# Revit family: CENTUM Winkel 3-Loch, quer ab XL100
name_source: partatom
category: HLS-Bauteile
revit_build: Autodesk Revit 2017 (Build: 20190507_1515(x64)
units: mm (PartAtom-declared; Revit-internal decimal feet)

## family parameters
Arbeitsebenenbasiert = Ja
Beim Laden mit Abzugskörper schneiden = Nein
Bemaßung runder Anschluss = Durchmesser verwenden
Gemeinsam genutzt = Ja
Immer vertikal = Nein
Raumberechnungspunkt = Nein
Teiletyp = Normal

## types (2) — shared parameters
B = 90 mm  [stored 0.295276 ft]
Breite Material = 90 mm
Fabrikat = MEFA
Firma = MEFA Befestigungs- und Montagesysteme GmbH
Gewicht = 1.74 kg
Gewicht pro Bauteil = 1.74 kg
Kurztext2 = 90 ° Schenkel 150 x 100 mm
L1 = 150 mm
L2 = 100 mm  [stored 0.328084 ft]
Langloch = 14x40 mm
Länge Schenkel 1 = 150 mm
Länge Schenkel 2 = 100 mm  [stored 0.328084 ft]
Material = Stahl
Mengeneinheit = St
Oberflaeche = feuerstückverzinkt
Profil = CENTUM
S = 10 mm  [stored 0.0328084 ft]
Sicherheitsfaktor = 1.54
Stärke Material = 10 mm  [stored 0.0328084 ft]
Vorgabe-Ansicht = 1219 mm
Winkel = 90 °
vpe = 1 St
zero-valued in all types: max. Rohraußendurchmesser, min. Rohraußendurchmesser

## per-type parameters (varying)
| type | A | Artikelnummer | EAN | Kurztext1 | Profiltyp |
| CENTUM Winkel 3-Loch, quer XL100 | 50 mm  [stored 0.164042 ft] | 1640001012 | 4250928436849 | Winkel 3-Loch CENTUM XL 100 | XL 100 |
| CENTUM Winkel 3-Loch, quer XL120 | 60 mm  [stored 0.19685 ft] | 1641201012 | 4250928450432 | Winkel 3-Loch CENTUM XL 120 | XL 120 |

note: [stored X ft] marks values corroborated as IEEE doubles in the binary element streams (Revit-internal decimal feet)
